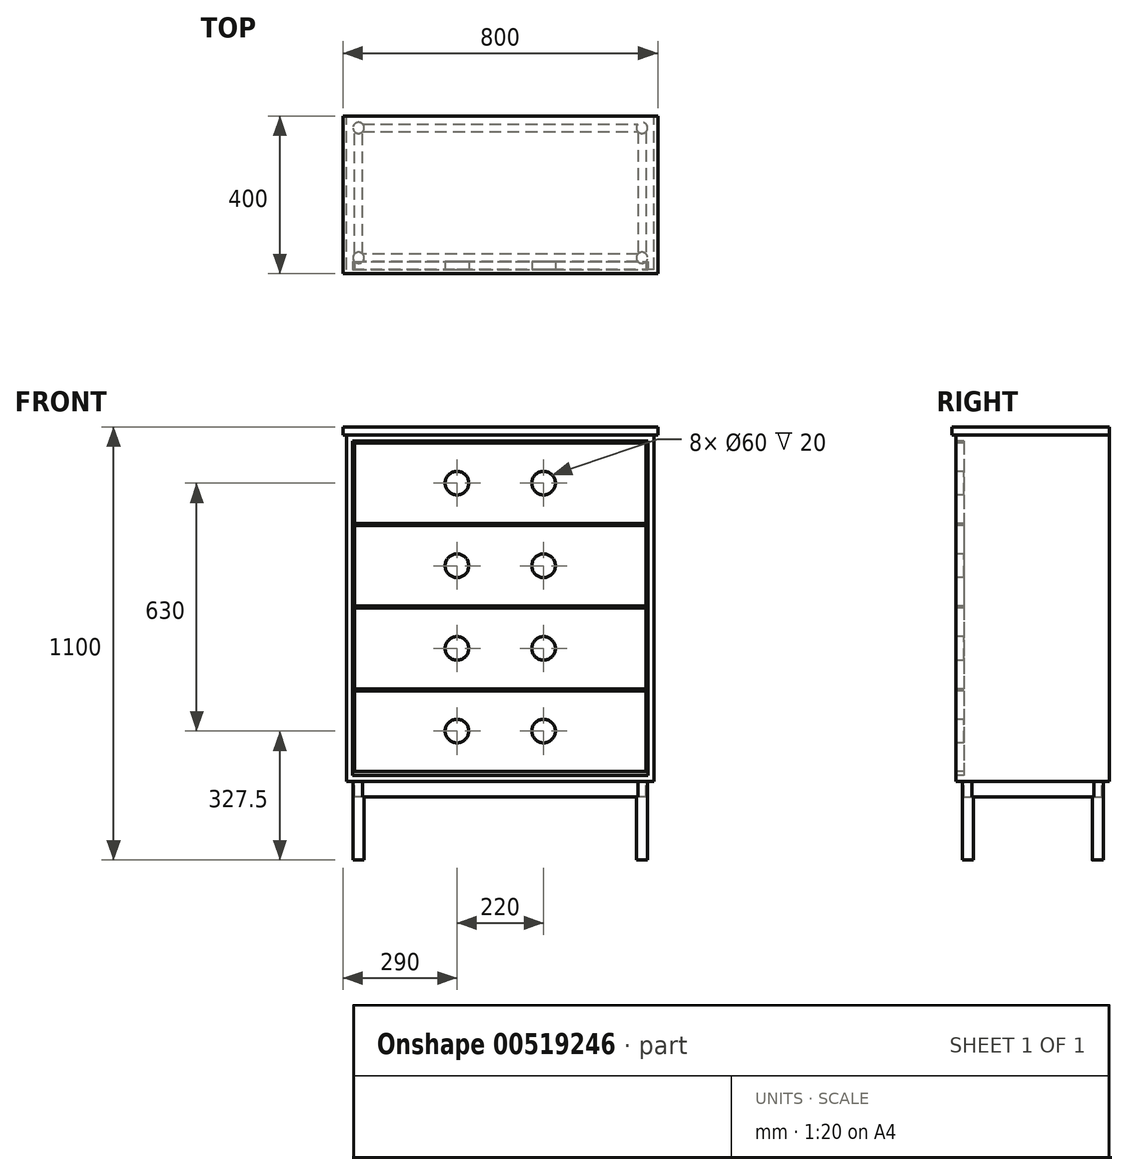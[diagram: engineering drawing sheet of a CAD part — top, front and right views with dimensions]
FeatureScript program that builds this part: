
annotation { "Feature Type Name" : "Feature", "Feature Type Description" : "" }
export const myFeature = defineFeature(function(context is Context, id is Id, definition is map)
    precondition{}
    {
        {
            var Q0;
            Q0=qCreatedBy(makeId("Right.planeOp"),FACE);
            var sketch = newSketch(context, id + "F0", { "sketchPlane" : qUnion([Q0])});
            skLineSegment(sketch, "E0.bottom", {"start": v(0, 0) * mm, "end": v(390, 0) * mm});
            skLineSegment(sketch, "E0.top", {"start": v(0, 900) * mm, "end": v(390, 900) * mm});
            skLineSegment(sketch, "E0.left", {"start": v(0, 0) * mm, "end": v(0, 900) * mm});
            skLineSegment(sketch, "E0.right", {"start": v(390, 0) * mm, "end": v(390, 900) * mm});
            skSolve(sketch);
        }
        {
            var Q0;
            Q0=qSketchRegion(id+"F0",true);
            extrude(context, id + "F1", {"entities" : qUnion([Q0]), "depth" : 780 * mm, "offsetDistance" : 25 * mm});
        }
        {
            var Q0;
            Q0=makeQuery(id+"F1.opExtrude","SWEPT_FACE",FACE,{"disambiguationData":[OSD([sQuery(id+"F0.wireOp",EDGE,"E0.top")])]});
            var sketch = newSketch(context, id + "F2", { "sketchPlane" : qUnion([Q0])});
            skLineSegment(sketch, "E1.0", {"start": v(-10, 390) * mm, "end": v(-10, -10) * mm});
            skLineSegment(sketch, "E1.2", {"start": v(790, -10) * mm, "end": v(790, 390) * mm});
            skLineSegment(sketch, "E1.3", {"start": v(-10, -10) * mm, "end": v(790, -10) * mm});
            skLineSegment(sketch, "E2", {"start": v(-10, 390) * mm, "end": v(790, 390) * mm});
            skSolve(sketch);
        }
        {
            var Q0;
            Q0=qSketchRegion(id+"F2",true);
            extrude(context, id + "F3", {"entities" : qUnion([Q0]), "operationType" : NewBodyOperationType.ADD, "oppositeDirection" : true, "depth" : 20 * mm, "offsetDistance" : 25 * mm});
        }
        {
            var Q0;
            Q0=makeQuery(id+"F1.opExtrude","SWEPT_FACE",FACE,{"disambiguationData":[OSD([sQuery(id+"F0.wireOp",EDGE,"E0.left")])]});
            var sketch = newSketch(context, id + "F4", { "sketchPlane" : qUnion([Q0])});
            skLineSegment(sketch, "E3.bottom", {"start": v(20, 860) * mm, "end": v(760, 860) * mm});
            skLineSegment(sketch, "E3.top", {"start": v(20, 655) * mm, "end": v(760, 655) * mm});
            skLineSegment(sketch, "E3.left", {"start": v(20, 860) * mm, "end": v(20, 655) * mm});
            skLineSegment(sketch, "E3.right", {"start": v(760, 860) * mm, "end": v(760, 655) * mm});
            skLineSegment(sketch, "E4.0.1.0", {"start": v(760, 650) * mm, "end": v(760, 445) * mm});
            skLineSegment(sketch, "E4.0.1.1", {"start": v(20, 650) * mm, "end": v(20, 445) * mm});
            skLineSegment(sketch, "E4.0.1.2", {"start": v(20, 445) * mm, "end": v(760, 445) * mm});
            skLineSegment(sketch, "E4.0.1.3", {"start": v(20, 650) * mm, "end": v(760, 650) * mm});
            skLineSegment(sketch, "E4.0.2.0", {"start": v(760, 440) * mm, "end": v(760, 235) * mm});
            skLineSegment(sketch, "E4.0.2.1", {"start": v(20, 440) * mm, "end": v(20, 235) * mm});
            skLineSegment(sketch, "E4.0.2.2", {"start": v(20, 235) * mm, "end": v(760, 235) * mm});
            skLineSegment(sketch, "E4.0.2.3", {"start": v(20, 440) * mm, "end": v(760, 440) * mm});
            skLineSegment(sketch, "E4.0.3.0", {"start": v(760, 230) * mm, "end": v(760, 25) * mm});
            skLineSegment(sketch, "E4.0.3.1", {"start": v(20, 230) * mm, "end": v(20, 25) * mm});
            skLineSegment(sketch, "E4.0.3.2", {"start": v(20, 25) * mm, "end": v(760, 25) * mm});
            skLineSegment(sketch, "E4.0.3.3", {"start": v(20, 230) * mm, "end": v(760, 230) * mm});
            skLineSegment(sketch, "E4.direction1", {"start": v(20, 655) * mm, "end": v(180, 655) * mm, "construction": true});
            skLineSegment(sketch, "E4.direction2", {"start": v(20, 655) * mm, "end": v(20, 445) * mm, "construction": true});
            skLineSegment(sketch, "E5.bottom", {"start": v(15, 865) * mm, "end": v(765, 865) * mm});
            skLineSegment(sketch, "E5.top", {"start": v(15, 15) * mm, "end": v(765, 15) * mm});
            skLineSegment(sketch, "E5.left", {"start": v(15, 865) * mm, "end": v(15, 15) * mm});
            skLineSegment(sketch, "E5.right", {"start": v(765, 865) * mm, "end": v(765, 15) * mm});
            skLineSegment(sketch, "E6", {"start": v(20, 757.5) * mm, "end": v(760, 757.5) * mm, "construction": true});
            skCircle(sketch, "E7", {"center": v(280, 757.5) * mm, "radius": 30 * mm});
            skCircle(sketch, "E8", {"center": v(500, 757.5) * mm, "radius": 30 * mm});
            skCircle(sketch, "E9.0.1.0", {"center": v(280, 547.5) * mm, "radius": 30 * mm});
            skCircle(sketch, "E9.0.1.1", {"center": v(500, 547.5) * mm, "radius": 30 * mm});
            skCircle(sketch, "E9.0.2.0", {"center": v(280, 337.5) * mm, "radius": 30 * mm});
            skCircle(sketch, "E9.0.2.1", {"center": v(500, 337.5) * mm, "radius": 30 * mm});
            skCircle(sketch, "E9.0.3.0", {"center": v(280, 127.5) * mm, "radius": 30 * mm});
            skCircle(sketch, "E9.0.3.1", {"center": v(500, 127.5) * mm, "radius": 30 * mm});
            skLineSegment(sketch, "E9.direction1", {"start": v(280, 757.5) * mm, "end": v(385, 757.5) * mm, "construction": true});
            skLineSegment(sketch, "E9.direction2", {"start": v(280, 757.5) * mm, "end": v(280, 547.5) * mm, "construction": true});
            skSolve(sketch);
        }
        {
            var Q0;
            Q0=qSketchRegion(id+"F4",true);
            var Q1;
            Q1=makeQuery(id+"F4.imprint","IMPRINT",FACE,{"disambiguationData":[TD([[makeQuery(id+"F4.imprint","IMPRINT",EDGE,{"derivedFrom":sQuery(id+"F4.wireOp",EDGE,"E7")}),1.0]])]});
            var Q2;
            Q2=makeQuery(id+"F4.imprint","IMPRINT",FACE,{"disambiguationData":[TD([[makeQuery(id+"F4.imprint","IMPRINT",EDGE,{"derivedFrom":sQuery(id+"F4.wireOp",EDGE,"E8")}),1.0]])]});
            var Q3;
            Q3=makeQuery(id+"F4.imprint","IMPRINT",FACE,{"disambiguationData":[TD([[makeQuery(id+"F4.imprint","IMPRINT",EDGE,{"derivedFrom":sQuery(id+"F4.wireOp",EDGE,"E9.0.1.0")}),1.0]])]});
            var Q4;
            Q4=makeQuery(id+"F4.imprint","IMPRINT",FACE,{"disambiguationData":[TD([[makeQuery(id+"F4.imprint","IMPRINT",EDGE,{"derivedFrom":sQuery(id+"F4.wireOp",EDGE,"E9.0.1.1")}),1.0]])]});
            var Q5;
            Q5=makeQuery(id+"F4.imprint","IMPRINT",FACE,{"disambiguationData":[TD([[makeQuery(id+"F4.imprint","IMPRINT",EDGE,{"derivedFrom":sQuery(id+"F4.wireOp",EDGE,"E9.0.2.0")}),1.0]])]});
            var Q6;
            Q6=makeQuery(id+"F4.imprint","IMPRINT",FACE,{"disambiguationData":[TD([[makeQuery(id+"F4.imprint","IMPRINT",EDGE,{"derivedFrom":sQuery(id+"F4.wireOp",EDGE,"E9.0.2.1")}),1.0]])]});
            var Q7;
            Q7=makeQuery(id+"F4.imprint","IMPRINT",FACE,{"disambiguationData":[TD([[makeQuery(id+"F4.imprint","IMPRINT",EDGE,{"derivedFrom":sQuery(id+"F4.wireOp",EDGE,"E9.0.3.0")}),1.0]])]});
            var Q8;
            Q8=makeQuery(id+"F4.imprint","IMPRINT",FACE,{"disambiguationData":[TD([[makeQuery(id+"F4.imprint","IMPRINT",EDGE,{"derivedFrom":sQuery(id+"F4.wireOp",EDGE,"E9.0.3.1")}),1.0]])]});
            extrude(context, id + "F5", {"entities" : qUnion([Q0, Q1, Q2, Q3, Q4, Q5, Q6, Q7, Q8]), "operationType" : NewBodyOperationType.REMOVE, "oppositeDirection" : true, "depth" : 20 * mm, "offsetDistance" : 25 * mm});
        }
        {
            var Q0;
            Q0=makeQuery(id+"F1.opExtrude","SWEPT_FACE",FACE,{"disambiguationData":[OSD([sQuery(id+"F0.wireOp",EDGE,"E0.bottom")])]});
            var sketch = newSketch(context, id + "F6", { "sketchPlane" : qUnion([Q0])});
            skLineSegment(sketch, "E10.0", {"start": v(20, -20) * mm, "end": v(20, -370) * mm});
            skLineSegment(sketch, "E10.1", {"start": v(760, -20) * mm, "end": v(20, -20) * mm});
            skLineSegment(sketch, "E10.2", {"start": v(760, -370) * mm, "end": v(760, -20) * mm});
            skLineSegment(sketch, "E10.3", {"start": v(20, -370) * mm, "end": v(760, -370) * mm});
            skLineSegment(sketch, "E11.0", {"start": v(40, -40) * mm, "end": v(40, -350) * mm});
            skLineSegment(sketch, "E11.1", {"start": v(740, -40) * mm, "end": v(40, -40) * mm});
            skLineSegment(sketch, "E11.2", {"start": v(740, -350) * mm, "end": v(740, -40) * mm});
            skLineSegment(sketch, "E11.3", {"start": v(40, -350) * mm, "end": v(740, -350) * mm});
            skSolve(sketch);
        }
        {
            var Q0;
            Q0=qSketchRegion(id+"F6",true);
            extrude(context, id + "F7", {"entities" : qUnion([Q0]), "operationType" : NewBodyOperationType.ADD, "depth" : 40 * mm, "offsetDistance" : 25 * mm});
        }
        {
            var Q0;
            {var subQ1=sQuery(id+"F0.wireOp",EDGE,"E0.left");var subQ3=sQuery(id+"F0.wireOp",EDGE,"E0.bottom");Q0=makeQuery(id+"F7.boolean.opBoolean","SPLIT",FACE,{"disambiguationData":[TD([makeQuery(id+"F1.opExtrude","SWEPT_FACE",FACE,{"disambiguationData":[OSD([subQ1])]})])],"derivedFrom":makeQuery(id+"F1.opExtrude","SWEPT_FACE",FACE,{"disambiguationData":[OSD([subQ3])]})});}
            var sketch = newSketch(context, id + "F8", { "sketchPlane" : qUnion([Q0])});
            skLineSegment(sketch, "E12", {"start": v(20, -20) * mm, "end": v(40, -40) * mm, "construction": true});
            skCircle(sketch, "E13", {"center": v(30, -30) * mm, "radius": 14.14 * mm});
            skLineSegment(sketch, "E14", {"start": v(390, -20) * mm, "end": v(390, -370) * mm, "construction": true});
            skCircle(sketch, "E15.MirrorC", {"center": v(750, -30) * mm, "radius": 14.14 * mm});
            skLineSegment(sketch, "E16", {"start": v(20, -195) * mm, "end": v(760, -195) * mm, "construction": true});
            skCircle(sketch, "E17.MirrorC", {"center": v(30, -360) * mm, "radius": 14.14 * mm});
            skCircle(sketch, "E18.MirrorC", {"center": v(750, -360) * mm, "radius": 14.14 * mm});
            skSolve(sketch);
        }
        {
            var Q0;
            Q0=qSketchRegion(id+"F8",true);
            extrude(context, id + "F9", {"entities" : qUnion([Q0]), "operationType" : NewBodyOperationType.ADD, "depth" : 200 * mm, "offsetDistance" : 25 * mm});
        }
    });
